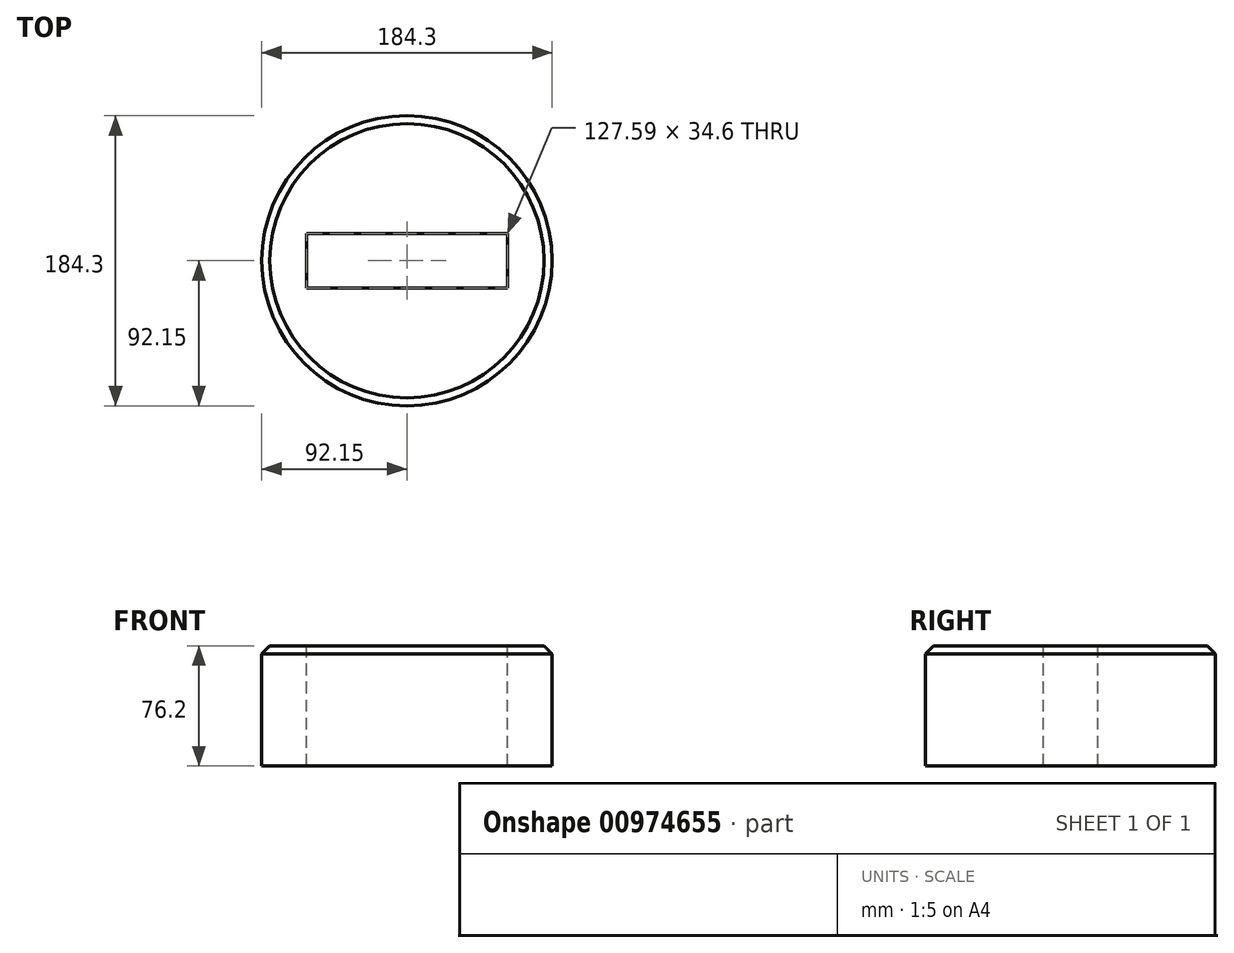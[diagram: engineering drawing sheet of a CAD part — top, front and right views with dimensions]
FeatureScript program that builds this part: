
annotation { "Feature Type Name" : "Feature", "Feature Type Description" : "" }
export const myFeature = defineFeature(function(context is Context, id is Id, definition is map)
    precondition{}
    {
        {
            var Q0;
            Q0=qCreatedBy(makeId("Top.planeOp"),FACE);
            var sketch = newSketch(context, id + "F0", { "sketchPlane" : qUnion([Q0])});
            skCircle(sketch, "E0", {"center": v(0, 0) * mm, "radius": 92.15 * mm});
            skSolve(sketch);
        }
        {
            var Q0;
            Q0=makeQuery(id+"F0.imprint","IMPRINT",FACE,{"disambiguationData":[TD([[makeQuery(id+"F0.imprint","IMPRINT",EDGE,{"derivedFrom":sQuery(id+"F0.wireOp",EDGE,"E0")}),1.0]])]});
            extrude(context, id + "F1", {"entities" : qUnion([Q0]), "depth" : 76.2 * mm, "offsetDistance" : 25.4 * mm});
        }
        {
            var Q0;
            Q0=makeQuery(id+"F1.opExtrude","CAP_EDGE",EDGE,{"disambiguationData":[OSD([sQuery(id+"F0.wireOp",EDGE,"E0")])],"isStart":false});
            chamfer(context, id + "F2", {"entities" : qUnion([Q0]), "width" : 5.08 * mm, "tangentPropagation" : true});
        }
        {
            var Q0;
            Q0=makeQuery(id+"F1.opExtrude","CAP_FACE",FACE,{"disambiguationData":[OSD([sQuery(id+"F0.wireOp",EDGE,"E0")])],"isStart":false});
            var sketch = newSketch(context, id + "F3", { "sketchPlane" : qUnion([Q0])});
            skLineSegment(sketch, "E1.bottom", {"start": v(-63.8, 17.3) * mm, "end": v(63.8, 17.3) * mm});
            skLineSegment(sketch, "E1.top", {"start": v(-63.8, -17.3) * mm, "end": v(63.8, -17.3) * mm});
            skLineSegment(sketch, "E1.left", {"start": v(-63.8, 17.3) * mm, "end": v(-63.8, -17.3) * mm});
            skLineSegment(sketch, "E1.right", {"start": v(63.8, 17.3) * mm, "end": v(63.8, -17.3) * mm});
            skPoint(sketch, "E1.middle", {"position": v(0, 0) * mm});
            skSolve(sketch);
        }
        {
            var Q0;
            Q0=makeQuery(id+"F3.imprint","IMPRINT",FACE,{"disambiguationData":[TD([[makeQuery(id+"F3.imprint","IMPRINT",EDGE,{"derivedFrom":sQuery(id+"F3.wireOp",EDGE,"E1.bottom")}),-1.0]])]});
            extrude(context, id + "F4", {"entities" : qUnion([Q0]), "operationType" : NewBodyOperationType.REMOVE, "oppositeDirection" : true, "depth" : 115.57 * mm, "offsetDistance" : 25.4 * mm});
        }
    });
